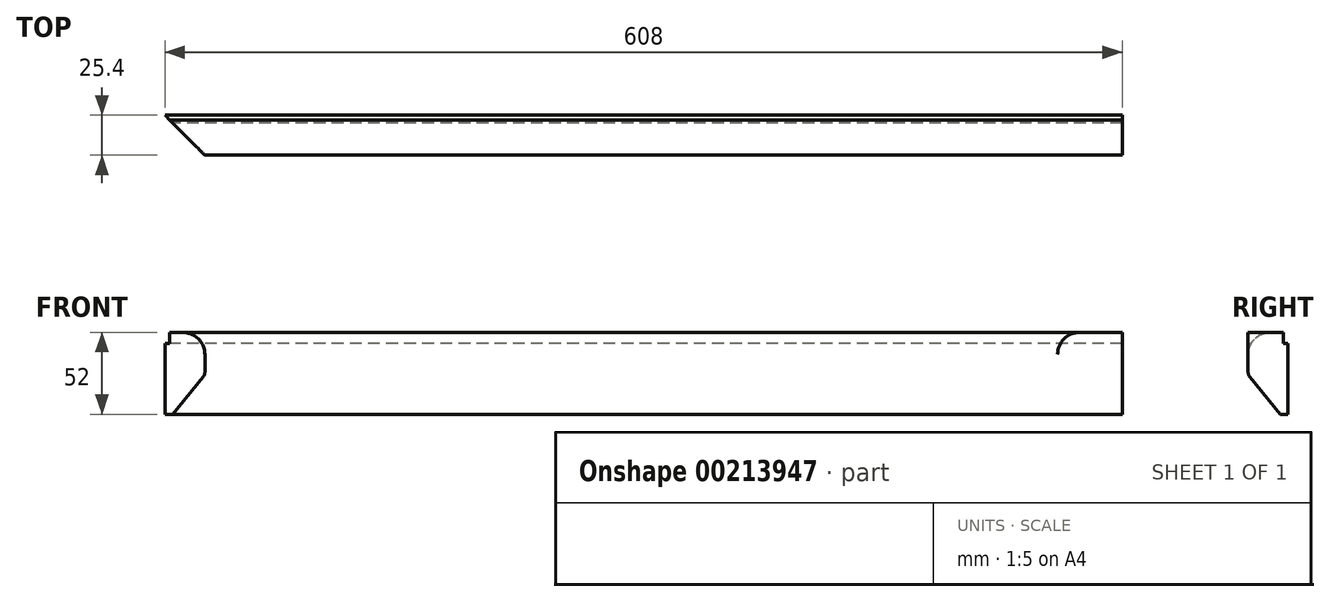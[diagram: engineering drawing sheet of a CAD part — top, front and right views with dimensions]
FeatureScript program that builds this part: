
annotation { "Feature Type Name" : "Feature", "Feature Type Description" : "" }
export const myFeature = defineFeature(function(context is Context, id is Id, definition is map)
    precondition{}
    {
        {
            var Q0;
            Q0=qCreatedBy(makeId("Right.planeOp"),FACE);
            var sketch = newSketch(context, id + "F0", { "sketchPlane" : qUnion([Q0])});
            skLineSegment(sketch, "E0.bottom", {"start": v(0, 0) * mm, "end": v(22.4, 0) * mm});
            skLineSegment(sketch, "E0.top", {"start": v(20.4, -52) * mm, "end": v(25.4, -52) * mm});
            skLineSegment(sketch, "E0.left", {"start": v(0, 0) * mm, "end": v(0, -27) * mm});
            skLineSegment(sketch, "E0.right", {"start": v(25.4, -7) * mm, "end": v(25.4, -52) * mm});
            skLineSegment(sketch, "E1", {"start": v(0, -27) * mm, "end": v(20.4, -52) * mm});
            skLineSegment(sketch, "E2.top", {"start": v(25.4, -7) * mm, "end": v(22.4, -7) * mm});
            skLineSegment(sketch, "E2.right", {"start": v(22.4, 0) * mm, "end": v(22.4, -7) * mm});
            skSolve(sketch);
        }
        {
            var Q0;
            Q0 = qSketchRegion(id + "F0", true);
            extrude(context, id + "F1", {"entities" : qUnion([Q0]), "depth" : 41 * mm, "hasSecondDirection" : true, "secondDirectionOppositeDirection" : true, "secondDirectionDepth" : 824 * mm});
        }
        {
            var Q0;
            Q0=qCreatedBy(makeId("Right.planeOp"),FACE);
            var sketch = newSketch(context, id + "F2", { "sketchPlane" : qUnion([Q0])});
            skPoint(sketch, "E3.start.orphan", {"position": v(-6.94, -10) * mm});
            skArc(sketch, "E4", {"start": v(14, 0) * mm, "mid": v(4.1, -4.1) * mm, "end": v(0, -14) * mm});
            skLineSegment(sketch, "E5", {"start": v(0, -14) * mm, "end": v(0, 13.54) * mm});
            skLineSegment(sketch, "E6", {"start": v(0, 13.54) * mm, "end": v(14, 13.54) * mm});
            skLineSegment(sketch, "E7", {"start": v(14, 0) * mm, "end": v(14, 13.54) * mm});
            skSolve(sketch);
        }
        {
            var Q0;
            Q0 = qSketchRegion(id + "F2", true);
            var Q1;
            Q1=sQuery(id+"F2.wireOp",EDGE,"E5");
            revolve(context, id + "F3", {"operationType" : NewBodyOperationType.REMOVE, "entities" : qUnion([Q0]), "axis" : qUnion([Q1]), "revolveType" : RevolveType.FULL});
        }
        {
            var Q0;
            Q0=makeQuery(id+"F1.opExtrude","CAP_FACE",FACE,{"disambiguationData":[OSD([sQuery(id+"F0.wireOp",EDGE,"E0.bottom"),sQuery(id+"F0.wireOp",EDGE,"E0.top"),sQuery(id+"F0.wireOp",EDGE,"E0.left"),sQuery(id+"F0.wireOp",EDGE,"E0.right")])],"isStart":true});
            var sketch = newSketch(context, id + "F4", { "sketchPlane" : qUnion([Q0])});
            skArc(sketch, "E8.0", {"start": v(-14, 0) * mm, "mid": v(-4.1, -4.1) * mm, "end": v(0, -14) * mm});
            skLineSegment(sketch, "E8.1", {"start": v(-14, 0) * mm, "end": v(-14, 13.54) * mm});
            skLineSegment(sketch, "E8.2", {"start": v(0, 13.54) * mm, "end": v(-14, 13.54) * mm});
            skLineSegment(sketch, "E8.3", {"start": v(0, -14) * mm, "end": v(0, 13.54) * mm});
            skSolve(sketch);
        }
        {
            var Q0;
            Q0 = qSketchRegion(id + "F4", true);
            var Q1;
            Q1=sQuery(id+"F2.wireOp",VERTEX,"E5.start");
            extrude(context, id + "F5", {"entities" : qUnion([Q0]), "operationType" : NewBodyOperationType.REMOVE, "endBound" : BoundingType.UP_TO_VERTEX, "oppositeDirection" : true, "endBoundEntityVertex" : qUnion([Q1]), "depth" : 25 * mm});
        }
        {
            var Q0;
            Q0=makeQuery(id+"F1.opExtrude","SWEPT_EDGE",EDGE,{"disambiguationData":[OSD([sQuery(id+"F0.wireOp",EDGE,"E0.left"),sQuery(id+"F0.wireOp",EDGE,"E1")])]});
            fillet(context, id + "F6", {"entities" : qUnion([Q0]), "radius" : 5 * mm, "tangentPropagation" : true, "allowEdgeOverflow" : false});
        }
        {
            var Q0;
            Q0=makeQuery(id+"F1.opExtrude","SWEPT_FACE",FACE,{"disambiguationData":[OSD([sQuery(id+"F0.wireOp",EDGE,"E0.bottom")])]});
            var sketch = newSketch(context, id + "F7", { "sketchPlane" : qUnion([Q0])});
            skLineSegment(sketch, "E9", {"start": v(-567, 25.4) * mm, "end": v(-520.65, -20.95) * mm});
            skLineSegment(sketch, "E10", {"start": v(-520.65, -20.95) * mm, "end": v(-858.55, -20.95) * mm});
            skLineSegment(sketch, "E11", {"start": v(-858.55, -20.95) * mm, "end": v(-858.55, 112.42) * mm});
            skLineSegment(sketch, "E12", {"start": v(-858.55, 112.42) * mm, "end": v(-818.42, 72.29) * mm});
            skLineSegment(sketch, "E13", {"start": v(-818.42, 72.29) * mm, "end": v(-567, 25.4) * mm});
            skSolve(sketch);
        }
        {
            var Q0;
            Q0 = qSketchRegion(id + "F7", true);
            extrude(context, id + "F8", {"entities" : qUnion([Q0]), "operationType" : NewBodyOperationType.REMOVE, "endBound" : BoundingType.THROUGH_ALL, "oppositeDirection" : true, "depth" : 25 * mm});
        }
    });
